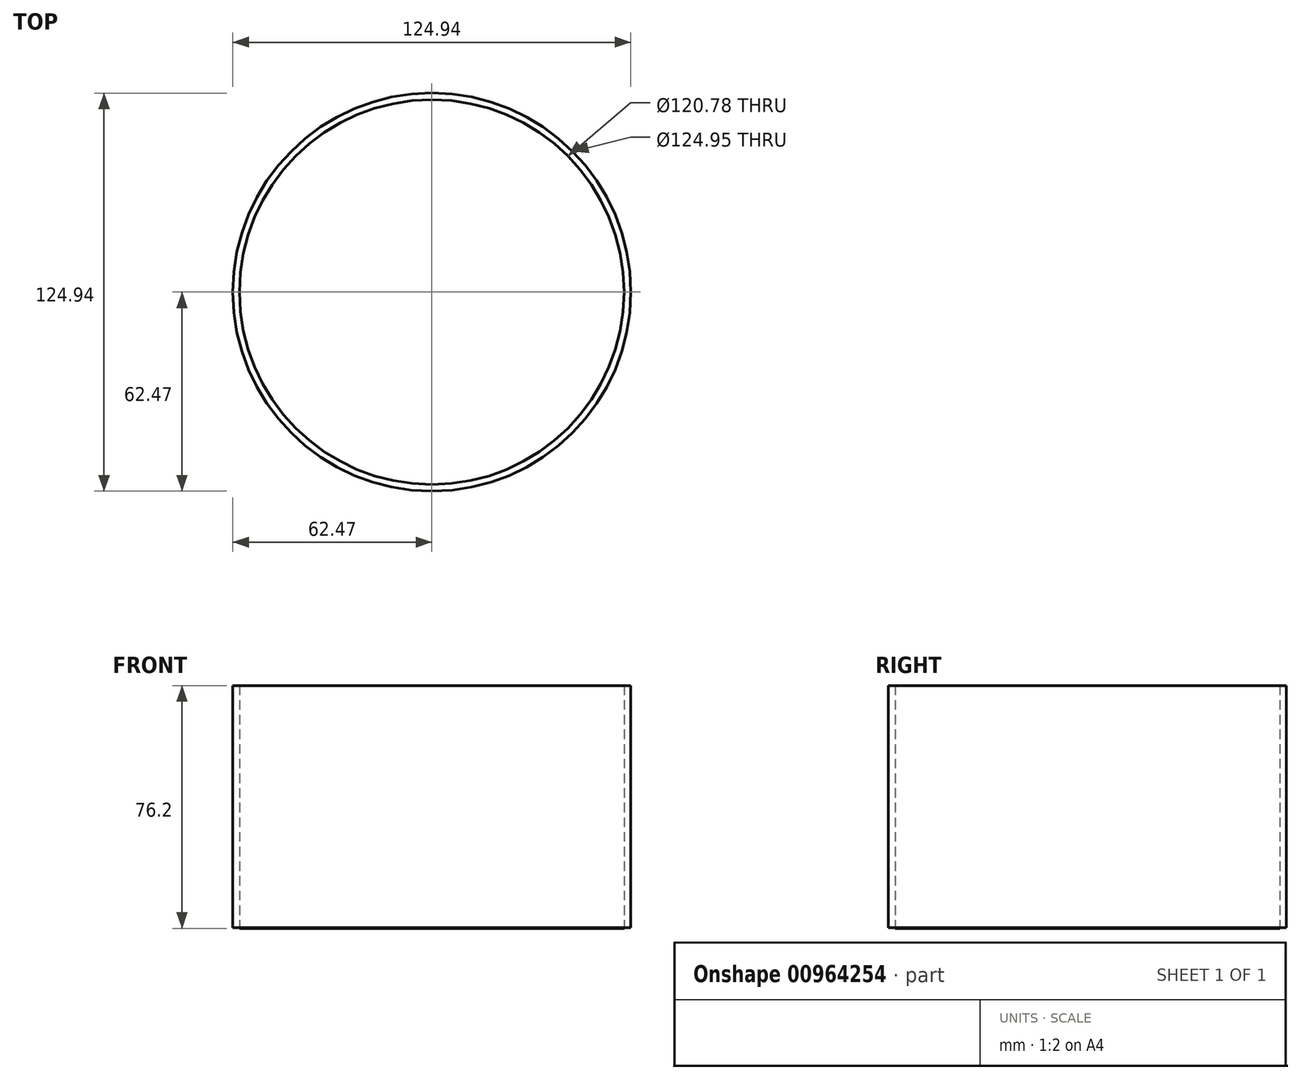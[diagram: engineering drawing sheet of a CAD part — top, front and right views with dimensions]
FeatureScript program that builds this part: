
annotation { "Feature Type Name" : "Feature", "Feature Type Description" : "" }
export const myFeature = defineFeature(function(context is Context, id is Id, definition is map)
    precondition{}
    {
        {
            var Q0;
            Q0=qCreatedBy(makeId("Top.planeOp"),FACE);
            var sketch = newSketch(context, id + "F0", { "sketchPlane" : qUnion([Q0])});
            skCircle(sketch, "E0", {"center": v(0, 0) * mm, "radius": 62.47 * mm});
            skSolve(sketch);
        }
        {
            var Q0;
            Q0 = qConstructionFilter(qBodyType(qCreatedBy(id + "F0" ,EDGE), BodyType.WIRE), ConstructionObject.NO);
            extrude(context, id + "F1", {"bodyType" : ToolBodyType.SURFACE, "surfaceEntities" : qUnion([Q0]), "oppositeDirection" : true, "depth" : 75.95 * mm, "offsetDistance" : 25.4 * mm});
        }
        {
            var Q0;
            Q0=qCreatedBy(makeId("Top.planeOp"),FACE);
            var sketch = newSketch(context, id + "F2", { "sketchPlane" : qUnion([Q0])});
            skCircle(sketch, "E1", {"center": v(0, 0) * mm, "radius": 60.39 * mm});
            skSolve(sketch);
        }
        {
            var Q0;
            Q0 = qSketchRegion(id + "F2", true);
            var Q1;
            Q1 = qConstructionFilter(qBodyType(qCreatedBy(id + "F2" ,EDGE), BodyType.WIRE), ConstructionObject.NO);
            extrude(context, id + "F3", {"entities" : qUnion([Q0]), "bodyType" : ToolBodyType.SURFACE, "surfaceEntities" : qUnion([Q1]), "oppositeDirection" : true, "depth" : 76.2 * mm, "offsetDistance" : 25.4 * mm});
        }
    });
